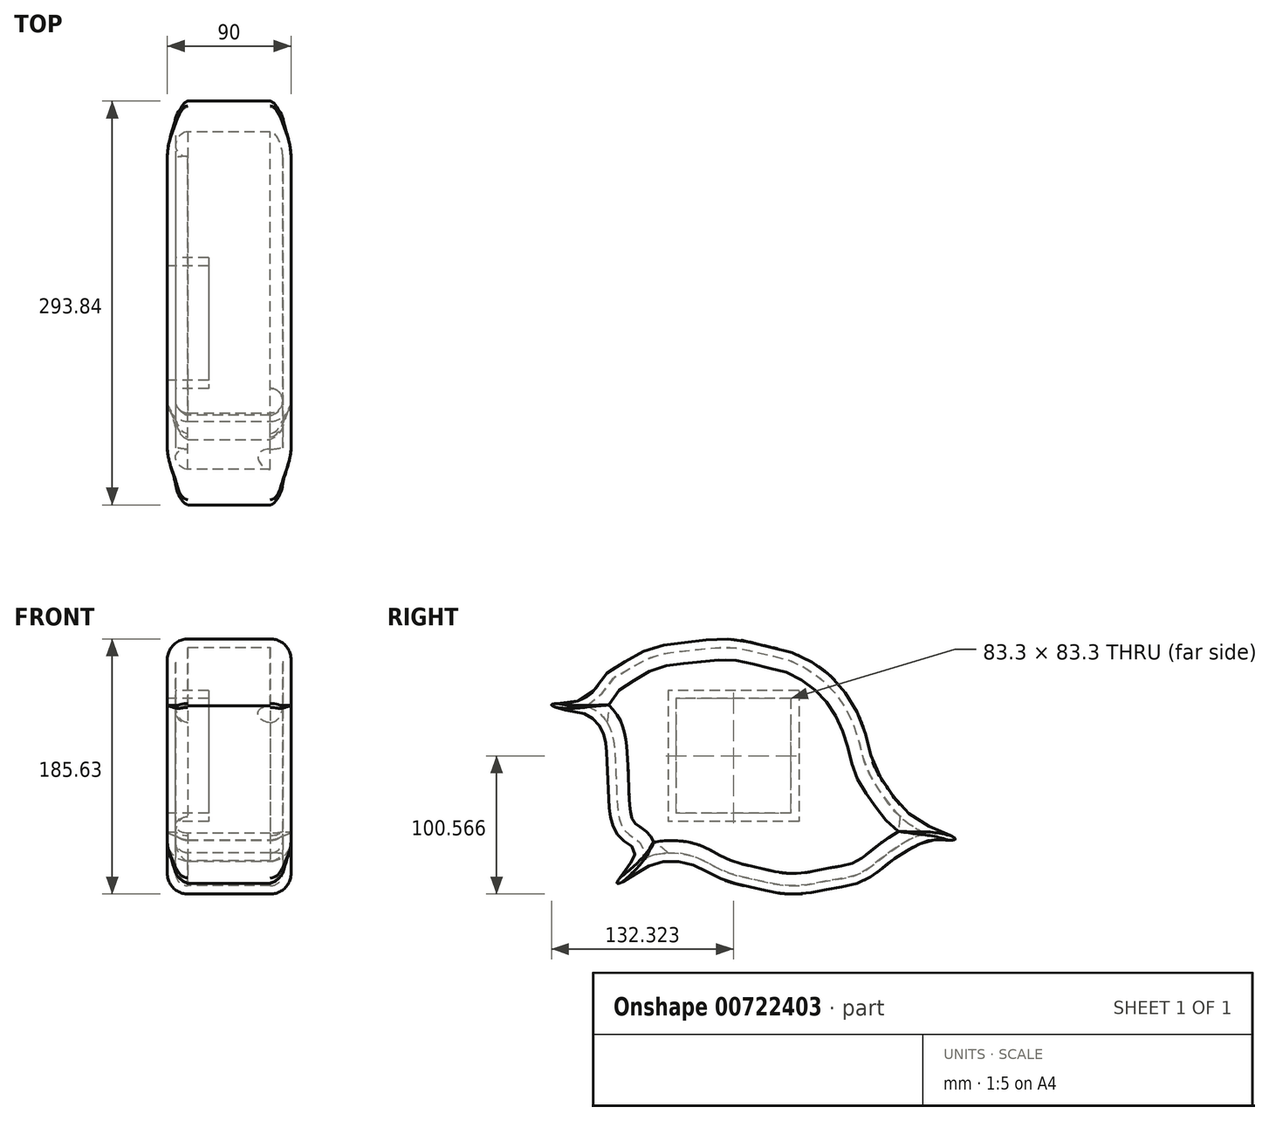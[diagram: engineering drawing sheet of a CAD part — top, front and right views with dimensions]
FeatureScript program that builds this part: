
annotation { "Feature Type Name" : "Feature", "Feature Type Description" : "" }
export const myFeature = defineFeature(function(context is Context, id is Id, definition is map)
    precondition{}
    {
        {
            var Q0;
            Q0=qCreatedBy(makeId("Right.planeOp"),FACE);
            var sketch = newSketch(context, id + "F0", { "sketchPlane" : qUnion([Q0])});
            skPoint(sketch, "E0.middle", {"position": v(0, 0) * mm});
            skFitSpline(sketch, "E1", {"points": [v(171.96, -37.84) * mm, v(161.29, -37.84) * mm, v(146.51, -43.58) * mm, v(129.28, -55.07) * mm, v(110.4, -68.2) * mm, v(87.42, -73.13) * mm, v(71, -76.41) * mm, v(50.48, -76.41) * mm, v(30.78, -72.3) * mm, v(9.44, -66.56) * mm, v(-10.26, -56.71) * mm, v(-22.57, -53.43) * mm, v(-38.98, -54.25) * mm, v(-51.3, -60.82) * mm, v(-67.71, -69.03) * mm, v(-54.58, -47.69) * mm, v(-61.15, -39.48) * mm, v(-70.17, -28.8) * mm, v(-73.46, -12.4) * mm, v(-74.28, 5.66) * mm, v(-75.1, 22.08) * mm, v(-79.2, 43.42) * mm, v(-91.51, 54.1) * mm, v(-104.65, 56.55) * mm, v(-115.32, 60.66) * mm, v(-102.18, 62.3) * mm, v(-85.77, 69.69) * mm, v(-75.1, 83.64) * mm, v(-61.97, 91.85) * mm, v(-48.83, 99.23) * mm, v(-33.24, 104.16) * mm, v(-11.08, 106.62) * mm, v(-5.33, 107.44) * mm, v(5.34, 108.26) * mm, v(18.47, 108.26) * mm, v(34.07, 104.98) * mm, v(48.02, 101.7) * mm, v(62.8, 97.6) * mm, v(77.57, 89.38) * mm, v(90.7, 78.71) * mm, v(100.55, 66.4) * mm, v(107.94, 53.27) * mm, v(114.5, 34.4) * mm, v(119.43, 16.33) * mm, v(129.28, 0) * mm, v(140.77, -14.85) * mm, v(156.36, -26.35) * mm, v(162.1, -28.8) * mm, v(167.85, -31.27) * mm, v(178.52, -37.02) * mm, v(171.96, -37.84) * mm]});
            skSolve(sketch);
        }
        {
            var Q0;
            Q0 = qSketchRegion(id + "F0", true);
            extrude(context, id + "F1", {"entities" : qUnion([Q0]), "depth" : 90 * mm, "offsetDistance" : 25.4 * mm});
        }
        {
            var Q0;
            Q0=makeQuery(id+"F1.opExtrude","CAP_EDGE",EDGE,{"disambiguationData":[OSD([sQuery(id+"F0.wireOp",EDGE,"E1")])],"isStart":false});
            fillet(context, id + "F2", {"entities" : qUnion([Q0]), "radius" : 15 * mm, "tangentPropagation" : true, "allowEdgeOverflow" : false});
        }
        {
            var Q0;
            Q0=makeQuery(id+"F1.opExtrude","CAP_EDGE",EDGE,{"disambiguationData":[OSD([sQuery(id+"F0.wireOp",EDGE,"E1")])],"isStart":true});
            fillet(context, id + "F3", {"entities" : qUnion([Q0]), "radius" : 15 * mm, "tangentPropagation" : true, "allowEdgeOverflow" : false});
        }
        {
            var Q0;
            Q0=makeQuery(id+"F1.opExtrude","CAP_FACE",FACE,{"disambiguationData":[OSD([sQuery(id+"F0.wireOp",EDGE,"E1")])],"isStart":true});
            var sketch = newSketch(context, id + "F4", { "sketchPlane" : qUnion([Q0])});
            skLineSegment(sketch, "E2.bottom", {"start": v(-58.65, 65.15) * mm, "end": v(24.65, 65.15) * mm});
            skLineSegment(sketch, "E2.top", {"start": v(-58.65, -18.15) * mm, "end": v(24.65, -18.15) * mm});
            skLineSegment(sketch, "E2.left", {"start": v(-58.65, 65.15) * mm, "end": v(-58.65, -18.15) * mm});
            skLineSegment(sketch, "E2.right", {"start": v(24.65, 65.15) * mm, "end": v(24.65, -18.15) * mm});
            skSolve(sketch);
        }
        {
            var Q0;
            Q0=makeQuery(id+"F4.imprint","IMPRINT",FACE,{"disambiguationData":[TD([[makeQuery(id+"F4.imprint","IMPRINT",EDGE,{"derivedFrom":sQuery(id+"F4.wireOp",EDGE,"E2.bottom")}),-1.0]])]});
            extrude(context, id + "F5", {"entities" : qUnion([Q0]), "operationType" : NewBodyOperationType.REMOVE, "oppositeDirection" : true, "depth" : 30 * mm, "offsetDistance" : 25.4 * mm});
        }
        {
            var Q0;
            Q0=makeQuery(id+"F5.boolean.opBoolean","COPY",FACE,{"derivedFrom":makeQuery(id+"F5.opExtrude","CAP_FACE",FACE,{"disambiguationData":[OSD([sQuery(id+"F4.wireOp",EDGE,"E2.bottom"),sQuery(id+"F4.wireOp",EDGE,"E2.top"),sQuery(id+"F4.wireOp",EDGE,"E2.left"),sQuery(id+"F4.wireOp",EDGE,"E2.right")])],"isStart":false})});
            shell(context, id + "F6", {"entities" : qUnion([Q0]), "thickness" : 6 * mm});
        }
    });
